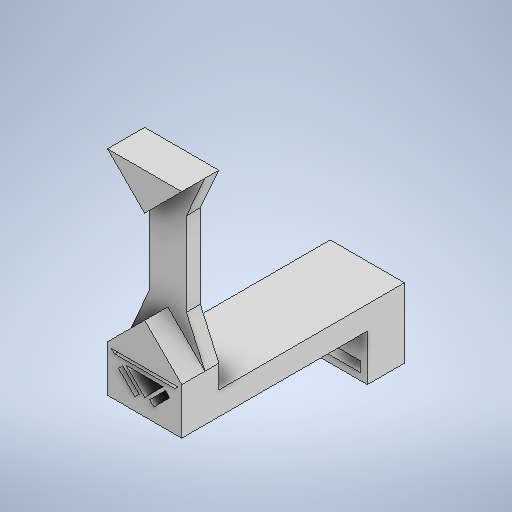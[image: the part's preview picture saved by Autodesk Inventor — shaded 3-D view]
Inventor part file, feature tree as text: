
AUTODESK INVENTOR PART (.ipt)
format: ipt  version: 2025.2 (Build 292293000, 293)  size: 333,824 bytes
history: native  units: mm
features: extrude x8, sketch x7
ambient origin geometry x8: Origin, YZ Plane, XZ Plane, XY Plane, X Axis, Y Axis, Z Axis, Center Point
bodies: Solid1 (feature_tree)
feature tree (15):
  sketch  "Sketch1"  dims[d0=20.0mm d1=16.0mm]
  extrude  "Extrusion1"  Depth=16.0mm
  extrude  "Extrusion2"  Depth=5.0mm TaperAngle=0.0deg
  extrude  "Extrusion3"  Depth=13.0mm
  extrude  "Extrusion4"  Depth=4.0mm
  extrude  "Extrusion5"  TaperAngle=45.0deg  [1 undecoded]
  extrude  "Extrusion6"  Depth=3.0mm TaperAngle=0.0deg
  extrude  "Extrusion7"  Depth=5.0mm
  extrude  "Extrusion8"  Depth=40.0mm TaperAngle=0.0deg
  sketch  "Sketch2"  dims[d3=5.0mm d4=5.0mm d5=0.0mm]
  sketch  "Sketch3"  dims[d7=1.5mm d9=13.0mm]
  sketch  "Sketch4"  dims[d10=4.0mm d11=0.0mm d12=36.0mm]
  sketch  "Sketch5"  dims[d13=90.0deg d14=45.0deg]
  sketch  "Sketch6"  dims[d15=5.0mm d16=0.0mm d17=3.0mm d18=0.0mm]
  sketch  "Sketch7"  dims[d19=10.0mm d20=0.0mm d21=5.0mm d22=40.0mm d23=0.0mm d24=8.0mm d25=10.0mm d26=0.0mm d27=16.0mm d28=5.0mm d29=1.5mm d30=1.5mm d31=13.0mm d32=2.2mm d33=3.0mm d34=0.0mm]
note: 1 required parameter value undecoded (feature->parameter linkage not recoverable at this tier; creation-order binding heuristic only, values carry confidence <= 0.55)
